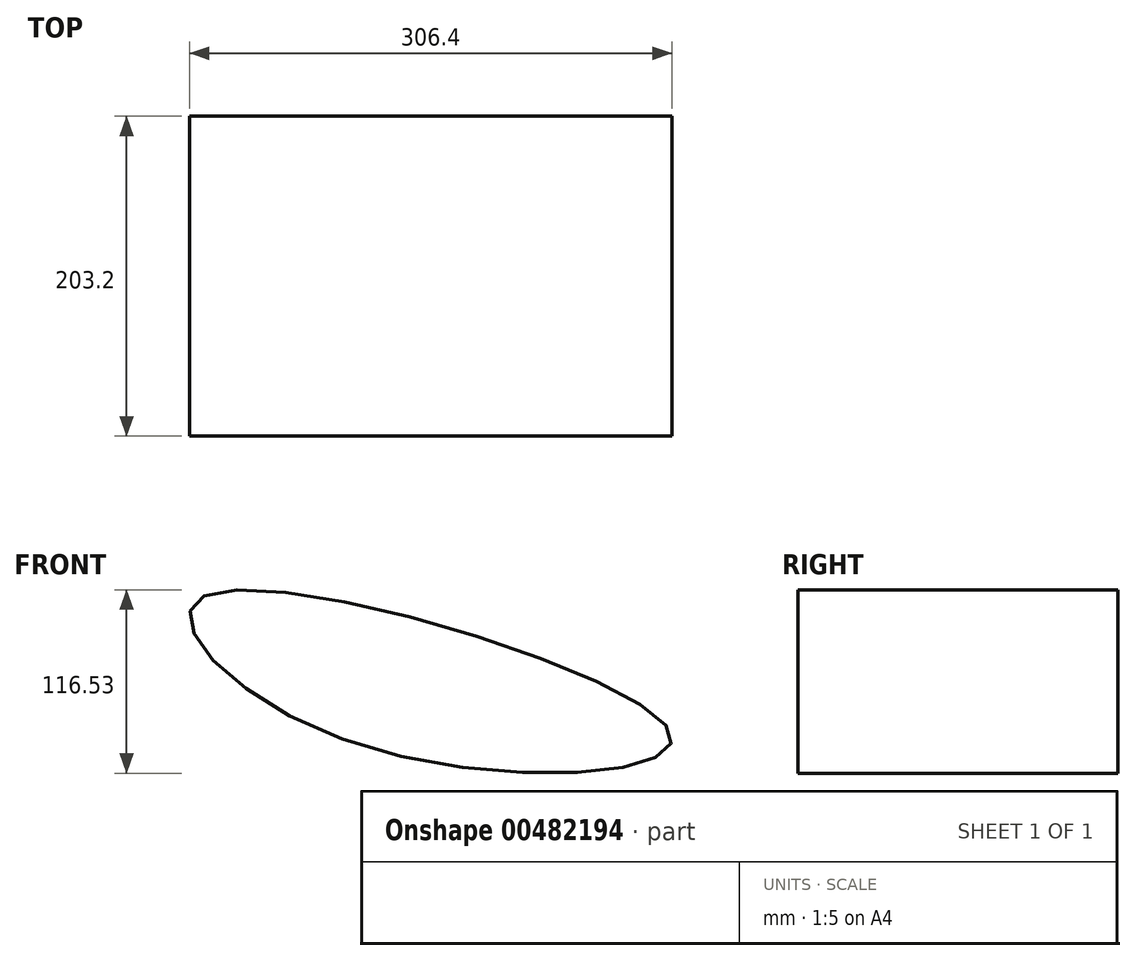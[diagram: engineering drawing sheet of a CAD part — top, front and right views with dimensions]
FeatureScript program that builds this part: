
annotation { "Feature Type Name" : "Feature", "Feature Type Description" : "" }
export const myFeature = defineFeature(function(context is Context, id is Id, definition is map)
    precondition{}
    {
        {
            var Q0;
            Q0=qCreatedBy(makeId("Front.planeOp"),FACE);
            var sketch = newSketch(context, id + "F0", { "sketchPlane" : qUnion([Q0])});
            skFitSpline(sketch, "E0", {"points": [v(-181.6, 45.32) * mm, v(114.48, -41.3) * mm, v(-97.34, -44.45) * mm, v(-181.6, 45.32) * mm]});
            skSolve(sketch);
        }
        {
            var Q0;
            Q0 = qSketchRegion(id + "F0", true);
            extrude(context, id + "F1", {"entities" : qUnion([Q0]), "depth" : 203.2 * mm});
        }
    });
